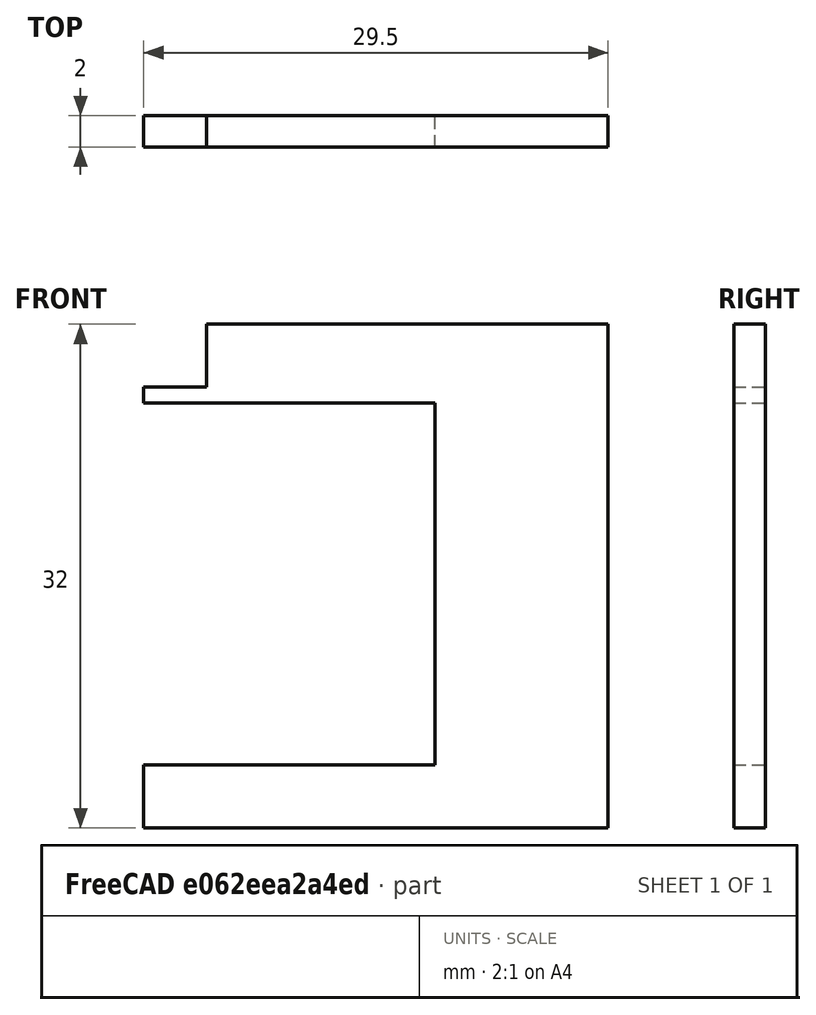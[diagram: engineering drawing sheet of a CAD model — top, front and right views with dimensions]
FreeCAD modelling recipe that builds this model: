
FCSTD DOCUMENT  (FreeCAD 0.14R3700 (Git))
Label: BIRR_fixMoteurPileAr
License: CC-BY 3.0
LicenseURL: http://creativecommons.org/licenses/by/3.0/
objects: Sketcher::SketchObject×1, Part::Extrusion×1, Part::Feature×1
note: 3 computed .brp shape members not serialized (recipe doc carries the construction recipe); baked Part::Feature solids carry a one-line shape summary decoded from their .brp

FEATURE [Sketcher::SketchObject] Sketch  label="fixMoteurPileAr"
  Placement = pos=(0,0,0) rot=(1,0,0;1.5708rad)
  sketch-geometry (10):
    g0: LineSegment StartX=18.5 StartY=11 StartZ=0 EndX=18.5 EndY=-12 EndZ=0
    g1: LineSegment StartX=4 StartY=16 StartZ=0 EndX=29.5 EndY=16 EndZ=0
    g2: LineSegment StartX=29.5 StartY=16 StartZ=0 EndX=29.5 EndY=-16 EndZ=0
    g3: LineSegment StartX=29.5 StartY=-16 StartZ=0 EndX=0 EndY=-16 EndZ=0
    g4: LineSegment StartX=18.5 StartY=11 StartZ=0 EndX=0 EndY=11 EndZ=0
    g5: LineSegment StartX=0 StartY=-12 StartZ=0 EndX=18.5 EndY=-12 EndZ=0
    g6: LineSegment StartX=0 StartY=-16 StartZ=0 EndX=0 EndY=-12 EndZ=0
    g7: LineSegment StartX=0 StartY=11 StartZ=0 EndX=0 EndY=12 EndZ=0
    g8: LineSegment StartX=0 StartY=12 StartZ=0 EndX=4 EndY=12 EndZ=0
    g9: LineSegment StartX=4 StartY=12 StartZ=0 EndX=4 EndY=16 EndZ=0
  constraints (30):
    c: Vertical(g0)
    c: Coincident(g1,g2)
    c: Coincident(g2,g3)
    c: Horizontal(g1)
    c: Horizontal(g3)
    c: Vertical(g2)
    c: DistanceX(g0,g2) = 11
    c: Symmetric(g2,g1,g-1)
    c: Coincident(g4,g0)
    c: Horizontal(g4)
    c: Coincident(g5,g0)
    c: Horizontal(g5)
    c: DistanceY(g2,g0) = 4
    c: DistanceY(g2) = -32
    c: DistanceY(g0,g1) = 5
    c: Coincident(g6,g3)
    c: Coincident(g6,g5)
    c: Vertical(g6)
    c: PointOnObject(g5,g-2)
    c: DistanceX(g4,g1) = 29.5
    c: Coincident(g7,g4)
    c: PointOnObject(g7,g-2)
    c: Vertical(g7)
    c: Coincident(g8,g7)
    c: Horizontal(g8)
    c: Coincident(g9,g8)
    c: Vertical(g9)
    c: DistanceY(g9) = 4
    c: Coincident(g1,g9)
    c: DistanceX(g8) = 4
FEATURE [Part::Extrusion] Extrude
  Base = -> Sketch
  Dir = (0,2,0)
  Solid = true
FEATURE [Part::Feature] Extrude001  label="fixMoteurPileAr_copy"
  shape: bbox 29.5 x 2 x 32 mm, 12 faces (baked)
